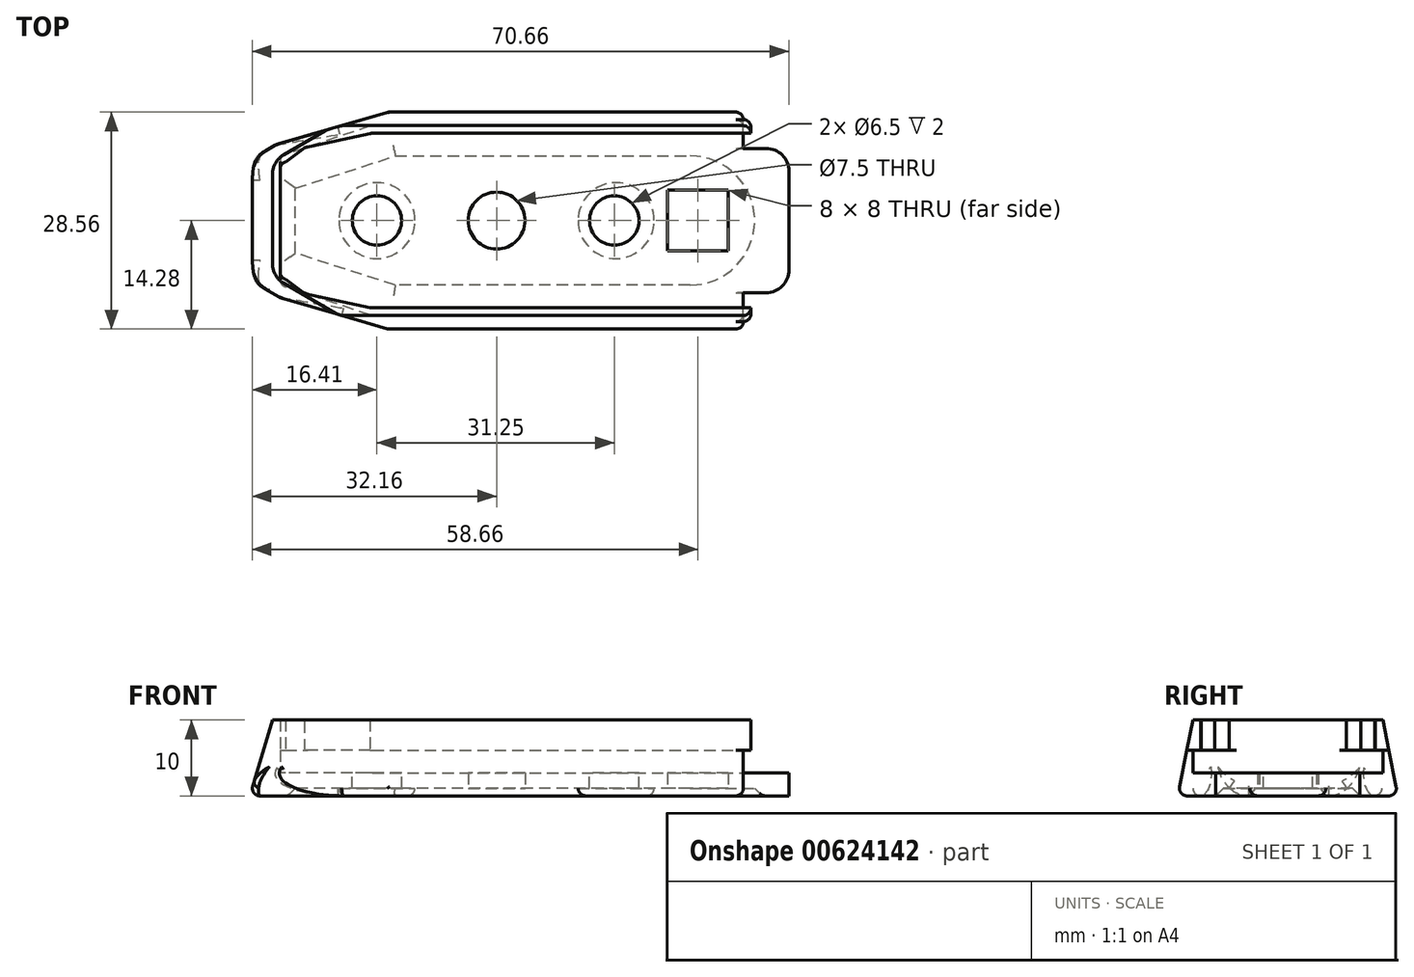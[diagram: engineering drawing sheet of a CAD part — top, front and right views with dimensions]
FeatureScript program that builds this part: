
annotation { "Feature Type Name" : "Feature", "Feature Type Description" : "" }
export const myFeature = defineFeature(function(context is Context, id is Id, definition is map)
    precondition{}
    {
        {
            var Q0;
            Q0=qCreatedBy(makeId("Top.planeOp"),FACE);
            var sketch = newSketch(context, id + "F0", { "sketchPlane" : qUnion([Q0])});
            skLineSegment(sketch, "E0.bottom", {"start": v(28.5, 14.5) * mm, "end": v(-16.5, 14.5) * mm});
            skLineSegment(sketch, "E0.left", {"start": v(35.5, 9.5) * mm, "end": v(35.5, 0) * mm});
            skLineSegment(sketch, "E0.right", {"start": v(-35.5, 9) * mm, "end": v(-35.5, 0) * mm});
            skPoint(sketch, "E0.middle", {"position": v(0, 0) * mm});
            skLineSegment(sketch, "E1", {"start": v(35.5, 0) * mm, "end": v(35.5, 9.5) * mm});
            skPoint(sketch, "E2.orphan", {"position": v(35.5, -14.5) * mm});
            skLineSegment(sketch, "E3", {"start": v(35.5, 9.5) * mm, "end": v(28.5, 9.5) * mm});
            skLineSegment(sketch, "E4", {"start": v(28.5, 9.5) * mm, "end": v(28.5, 14.5) * mm});
            skLineSegment(sketch, "E5", {"start": v(-35.5, 0) * mm, "end": v(-35.5, 9) * mm});
            skLineSegment(sketch, "E6", {"start": v(-35.5, 9) * mm, "end": v(-16.5, 14.5) * mm});
            skPoint(sketch, "E7.orphan", {"position": v(-35.5, 14.5) * mm});
            skPoint(sketch, "E8.orphan", {"position": v(-35.5, -14.5) * mm});
            skPoint(sketch, "E9.orphan", {"position": v(35.5, 14.5) * mm});
            skLineSegment(sketch, "E10.MirrorCS", {"start": v(-35.5, 0) * mm, "end": v(-35.5, -9) * mm});
            skLineSegment(sketch, "E11.MirrorCS", {"start": v(-35.5, -9) * mm, "end": v(-16.5, -14.5) * mm});
            skLineSegment(sketch, "E12.MirrorCS", {"start": v(28.5, -14.5) * mm, "end": v(-16.5, -14.5) * mm});
            skLineSegment(sketch, "E13.MirrorCS", {"start": v(28.5, -9.5) * mm, "end": v(28.5, -14.5) * mm});
            skLineSegment(sketch, "E14.MirrorCS", {"start": v(35.5, -9.5) * mm, "end": v(28.5, -9.5) * mm});
            skLineSegment(sketch, "E15.MirrorCS", {"start": v(35.5, 0) * mm, "end": v(35.5, -9.5) * mm});
            skSolve(sketch);
        }
        {
            var Q0;
            Q0 = qSketchRegion(id + "F0", true);
            extrude(context, id + "F1", {"entities" : qUnion([Q0]), "depth" : 3 * mm, "offsetDistance" : 25 * mm});
        }
        {
            var Q0;
            Q0=makeQuery(id+"F1.opExtrude","CAP_FACE",FACE,{"disambiguationData":[OSD([sQuery(id+"F0.wireOp",EDGE,"E1"),sQuery(id+"F0.wireOp",EDGE,"E3"),sQuery(id+"F0.wireOp",EDGE,"E4"),sQuery(id+"F0.wireOp",EDGE,"E0.bottom"),sQuery(id+"F0.wireOp",EDGE,"E5"),sQuery(id+"F0.wireOp",EDGE,"E6"),sQuery(id+"F0.wireOp",EDGE,"E10.MirrorCS"),sQuery(id+"F0.wireOp",EDGE,"E11.MirrorCS"),sQuery(id+"F0.wireOp",EDGE,"E12.MirrorCS"),sQuery(id+"F0.wireOp",EDGE,"E13.MirrorCS"),sQuery(id+"F0.wireOp",EDGE,"E14.MirrorCS"),sQuery(id+"F0.wireOp",EDGE,"E15.MirrorCS")])],"isStart":true});
            var sketch = newSketch(context, id + "F2", { "sketchPlane" : qUnion([Q0])});
            skPoint(sketch, "E16.endSnap0", {"position": v(-35.5, 0) * mm});
            skLineSegment(sketch, "E17", {"start": v(-30.5, 0) * mm, "end": v(-30.5, 5) * mm});
            skLineSegment(sketch, "E18", {"start": v(-30.5, 5) * mm, "end": v(-16.5, 9.5) * mm});
            skPoint(sketch, "E16.start.orphan", {"position": v(-35.5, 0) * mm});
            skLineSegment(sketch, "E19", {"start": v(-16.5, 9.5) * mm, "end": v(22.5, 9.5) * mm});
            skLineSegment(sketch, "E20.MirrorCS", {"start": v(-30.5, 0) * mm, "end": v(-30.5, -5) * mm});
            skLineSegment(sketch, "E21.MirrorCS", {"start": v(-30.5, -5) * mm, "end": v(-16.5, -9.5) * mm});
            skLineSegment(sketch, "E22.MirrorCS", {"start": v(-16.5, -9.5) * mm, "end": v(22.5, -9.5) * mm});
            skPoint(sketch, "E23.endSnap0", {"position": v(35.5, 0) * mm});
            skArc(sketch, "E24", {"start": v(22.5, -9.5) * mm, "mid": v(32, 0) * mm, "end": v(22.5, 9.5) * mm});
            skPoint(sketch, "E23.end.orphan", {"position": v(32, 0) * mm});
            skPoint(sketch, "E23.start.orphan", {"position": v(35.5, 0) * mm});
            skSolve(sketch);
        }
        {
            var Q0;
            Q0 = qSketchRegion(id + "F2", true);
            extrude(context, id + "F3", {"entities" : qUnion([Q0]), "operationType" : NewBodyOperationType.REMOVE, "oppositeDirection" : true, "depth" : 1 * mm, "offsetDistance" : 25 * mm});
        }
        {
            var Q0;
            Q0=makeQuery(id+"F3.boolean.opBoolean","COPY",EDGE,{"derivedFrom":makeQuery(id+"F3.opExtrude","CAP_EDGE",EDGE,{"disambiguationData":[OSD([sQuery(id+"F2.wireOp",EDGE,"E17"),sQuery(id+"F2.wireOp",EDGE,"E20.MirrorCS")])],"isStart":false})});
            var Q1;
            Q1=makeQuery(id+"F3.boolean.opBoolean","COPY",EDGE,{"derivedFrom":makeQuery(id+"F3.opExtrude","CAP_EDGE",EDGE,{"disambiguationData":[OSD([sQuery(id+"F2.wireOp",EDGE,"E18")])],"isStart":false})});
            var Q2;
            Q2=makeQuery(id+"F3.boolean.opBoolean","COPY",EDGE,{"derivedFrom":makeQuery(id+"F3.opExtrude","CAP_EDGE",EDGE,{"disambiguationData":[OSD([sQuery(id+"F2.wireOp",EDGE,"E21.MirrorCS")])],"isStart":false})});
            var Q3;
            Q3=makeQuery(id+"F3.boolean.opBoolean","COPY",EDGE,{"derivedFrom":makeQuery(id+"F3.opExtrude","CAP_EDGE",EDGE,{"disambiguationData":[OSD([sQuery(id+"F2.wireOp",EDGE,"E19")])],"isStart":false})});
            var Q4;
            Q4=makeQuery(id+"F3.boolean.opBoolean","COPY",EDGE,{"derivedFrom":makeQuery(id+"F3.opExtrude","CAP_EDGE",EDGE,{"disambiguationData":[OSD([sQuery(id+"F2.wireOp",EDGE,"E22.MirrorCS")])],"isStart":false})});
            var Q5;
            Q5=makeQuery(id+"F3.boolean.opBoolean","COPY",EDGE,{"derivedFrom":makeQuery(id+"F3.opExtrude","CAP_EDGE",EDGE,{"disambiguationData":[OSD([sQuery(id+"F2.wireOp",EDGE,"E24")])],"isStart":false})});
            chamfer(context, id + "F4", {"entities" : qUnion([Q0, Q1, Q2, Q3, Q4, Q5]), "width" : 1 * mm, "tangentPropagation" : true});
        }
        {
            var Q0;
            Q0=makeQuery(id+"F3.boolean.opBoolean","COPY",FACE,{"derivedFrom":makeQuery(id+"F3.opExtrude","CAP_FACE",FACE,{"disambiguationData":[OSD([sQuery(id+"F2.wireOp",EDGE,"E17"),sQuery(id+"F2.wireOp",EDGE,"E18"),sQuery(id+"F2.wireOp",EDGE,"E19"),sQuery(id+"F2.wireOp",EDGE,"E20.MirrorCS"),sQuery(id+"F2.wireOp",EDGE,"E21.MirrorCS"),sQuery(id+"F2.wireOp",EDGE,"E22.MirrorCS"),sQuery(id+"F2.wireOp",EDGE,"E24")])],"isStart":false})});
            var sketch = newSketch(context, id + "F5", { "sketchPlane" : qUnion([Q0])});
            skLineSegment(sketch, "E25", {"start": v(35.5, 0) * mm, "end": v(27.5, 0) * mm});
            skPoint(sketch, "E25.endSnap0", {"position": v(31, 0) * mm});
            skPoint(sketch, "E26.0.1.end.orphan", {"position": v(28.5, 14.5) * mm});
            skPoint(sketch, "E26.0.0.end.orphan", {"position": v(28.5, 9.5) * mm});
            skPoint(sketch, "E27.orphan", {"position": v(35.5, 9.5) * mm});
            skPoint(sketch, "E26.0.8.end.orphan", {"position": v(35.5, -9.5) * mm});
            skPoint(sketch, "E26.0.7.end.orphan", {"position": v(28.5, -9.5) * mm});
            skPoint(sketch, "E26.0.6.end.orphan", {"position": v(28.5, -14.5) * mm});
            skPoint(sketch, "E26.0.5.end.orphan", {"position": v(-16.5, -14.5) * mm});
            skPoint(sketch, "E26.0.4.end.orphan", {"position": v(-35.5, -9) * mm});
            skPoint(sketch, "E26.0.3.end.orphan", {"position": v(-35.5, 9) * mm});
            skPoint(sketch, "E26.0.3.start.orphan", {"position": v(-16.5, 14.5) * mm});
            skLineSegment(sketch, "E28", {"start": v(27.5, 0) * mm, "end": v(27.5, 4) * mm});
            skLineSegment(sketch, "E29", {"start": v(27.5, 4) * mm, "end": v(19.5, 4) * mm});
            skLineSegment(sketch, "E30", {"start": v(19.5, 4) * mm, "end": v(19.5, -4) * mm});
            skLineSegment(sketch, "E31", {"start": v(19.5, -4) * mm, "end": v(27.5, -4) * mm});
            skLineSegment(sketch, "E32", {"start": v(27.5, -4) * mm, "end": v(27.5, 0) * mm});
            skLineSegment(sketch, "E33", {"start": v(19.5, 0) * mm, "end": v(-3, 0) * mm});
            skCircle(sketch, "E34", {"center": v(-3, 0) * mm, "radius": 3.75 * mm});
            skSolve(sketch);
        }
        {
            var Q0;
            Q0 = qSketchRegion(id + "F5", true);
            extrude(context, id + "F6", {"entities" : qUnion([Q0]), "operationType" : NewBodyOperationType.REMOVE, "endBound" : BoundingType.THROUGH_ALL, "oppositeDirection" : true, "depth" : 25 * mm, "offsetDistance" : 25 * mm});
        }
        {
            var Q0;
            Q0=makeQuery(id+"F3.boolean.opBoolean","COPY",FACE,{"derivedFrom":makeQuery(id+"F3.opExtrude","CAP_FACE",FACE,{"disambiguationData":[OSD([sQuery(id+"F2.wireOp",EDGE,"E17"),sQuery(id+"F2.wireOp",EDGE,"E18"),sQuery(id+"F2.wireOp",EDGE,"E19"),sQuery(id+"F2.wireOp",EDGE,"E20.MirrorCS"),sQuery(id+"F2.wireOp",EDGE,"E21.MirrorCS"),sQuery(id+"F2.wireOp",EDGE,"E22.MirrorCS"),sQuery(id+"F2.wireOp",EDGE,"E24")])],"isStart":false})});
            var sketch = newSketch(context, id + "F7", { "sketchPlane" : qUnion([Q0])});
            skLineSegment(sketch, "E35", {"start": v(0.75, 0) * mm, "end": v(12.75, 0) * mm});
            skCircle(sketch, "E36", {"center": v(12.75, 0) * mm, "radius": 5 * mm});
            skLineSegment(sketch, "E37", {"start": v(-6.75, 0) * mm, "end": v(-18.75, 0) * mm});
            skCircle(sketch, "E38", {"center": v(-18.75, 0) * mm, "radius": 5 * mm});
            skSolve(sketch);
        }
        {
            var Q0;
            Q0 = qSketchRegion(id + "F7", true);
            var Q1;
            Q1=makeQuery(id+"F1.opExtrude","CAP_FACE",FACE,{"disambiguationData":[OSD([sQuery(id+"F0.wireOp",EDGE,"E1"),sQuery(id+"F0.wireOp",EDGE,"E3"),sQuery(id+"F0.wireOp",EDGE,"E4"),sQuery(id+"F0.wireOp",EDGE,"E0.bottom"),sQuery(id+"F0.wireOp",EDGE,"E5"),sQuery(id+"F0.wireOp",EDGE,"E6"),sQuery(id+"F0.wireOp",EDGE,"E10.MirrorCS"),sQuery(id+"F0.wireOp",EDGE,"E11.MirrorCS"),sQuery(id+"F0.wireOp",EDGE,"E12.MirrorCS"),sQuery(id+"F0.wireOp",EDGE,"E13.MirrorCS"),sQuery(id+"F0.wireOp",EDGE,"E14.MirrorCS"),sQuery(id+"F0.wireOp",EDGE,"E15.MirrorCS")])],"isStart":true});
            extrude(context, id + "F8", {"entities" : qUnion([Q0]), "operationType" : NewBodyOperationType.ADD, "endBound" : BoundingType.UP_TO_SURFACE, "depth" : 25 * mm, "endBoundEntityFace" : qUnion([Q1]), "offsetDistance" : 25 * mm});
        }
        {
            var Q0;
            Q0=makeQuery(id+"F8.opExtrude","CAP_EDGE",EDGE,{"disambiguationData":[OSD([sQuery(id+"F7.wireOp",EDGE,"E38")])],"isStart":false});
            var Q1;
            Q1=makeQuery(id+"F8.opExtrude","CAP_EDGE",EDGE,{"disambiguationData":[OSD([sQuery(id+"F7.wireOp",EDGE,"E36")])],"isStart":false});
            var Q2;
            Q2=makeQuery(id+"F4.opChamfer","BLEND_EDGE",EDGE,{"blendedFrom":[makeQuery(id+"F3.boolean.opBoolean","COPY",EDGE,{"derivedFrom":makeQuery(id+"F3.opExtrude","CAP_EDGE",EDGE,{"disambiguationData":[OSD([sQuery(id+"F2.wireOp",EDGE,"E19")])],"isStart":false})}),makeQuery(id+"F1.opExtrude","CAP_FACE",FACE,{"disambiguationData":[OSD([sQuery(id+"F0.wireOp",EDGE,"E1"),sQuery(id+"F0.wireOp",EDGE,"E3"),sQuery(id+"F0.wireOp",EDGE,"E4"),sQuery(id+"F0.wireOp",EDGE,"E0.bottom"),sQuery(id+"F0.wireOp",EDGE,"E5"),sQuery(id+"F0.wireOp",EDGE,"E6"),sQuery(id+"F0.wireOp",EDGE,"E10.MirrorCS"),sQuery(id+"F0.wireOp",EDGE,"E11.MirrorCS"),sQuery(id+"F0.wireOp",EDGE,"E12.MirrorCS"),sQuery(id+"F0.wireOp",EDGE,"E13.MirrorCS"),sQuery(id+"F0.wireOp",EDGE,"E14.MirrorCS"),sQuery(id+"F0.wireOp",EDGE,"E15.MirrorCS")])],"isStart":true})],"blendedInto":[makeQuery(id+"F1.opExtrude","CAP_FACE",FACE,{"disambiguationData":[OSD([sQuery(id+"F0.wireOp",EDGE,"E1"),sQuery(id+"F0.wireOp",EDGE,"E3"),sQuery(id+"F0.wireOp",EDGE,"E4"),sQuery(id+"F0.wireOp",EDGE,"E0.bottom"),sQuery(id+"F0.wireOp",EDGE,"E5"),sQuery(id+"F0.wireOp",EDGE,"E6"),sQuery(id+"F0.wireOp",EDGE,"E10.MirrorCS"),sQuery(id+"F0.wireOp",EDGE,"E11.MirrorCS"),sQuery(id+"F0.wireOp",EDGE,"E12.MirrorCS"),sQuery(id+"F0.wireOp",EDGE,"E13.MirrorCS"),sQuery(id+"F0.wireOp",EDGE,"E14.MirrorCS"),sQuery(id+"F0.wireOp",EDGE,"E15.MirrorCS")])],"isStart":true})]});
            var Q3;
            Q3=makeQuery(id+"F4.opChamfer","BLEND_EDGE",EDGE,{"blendedFrom":[makeQuery(id+"F3.boolean.opBoolean","COPY",EDGE,{"derivedFrom":makeQuery(id+"F3.opExtrude","CAP_EDGE",EDGE,{"disambiguationData":[OSD([sQuery(id+"F2.wireOp",EDGE,"E18")])],"isStart":false})}),makeQuery(id+"F1.opExtrude","CAP_FACE",FACE,{"disambiguationData":[OSD([sQuery(id+"F0.wireOp",EDGE,"E1"),sQuery(id+"F0.wireOp",EDGE,"E3"),sQuery(id+"F0.wireOp",EDGE,"E4"),sQuery(id+"F0.wireOp",EDGE,"E0.bottom"),sQuery(id+"F0.wireOp",EDGE,"E5"),sQuery(id+"F0.wireOp",EDGE,"E6"),sQuery(id+"F0.wireOp",EDGE,"E10.MirrorCS"),sQuery(id+"F0.wireOp",EDGE,"E11.MirrorCS"),sQuery(id+"F0.wireOp",EDGE,"E12.MirrorCS"),sQuery(id+"F0.wireOp",EDGE,"E13.MirrorCS"),sQuery(id+"F0.wireOp",EDGE,"E14.MirrorCS"),sQuery(id+"F0.wireOp",EDGE,"E15.MirrorCS")])],"isStart":true})],"blendedInto":[makeQuery(id+"F1.opExtrude","CAP_FACE",FACE,{"disambiguationData":[OSD([sQuery(id+"F0.wireOp",EDGE,"E1"),sQuery(id+"F0.wireOp",EDGE,"E3"),sQuery(id+"F0.wireOp",EDGE,"E4"),sQuery(id+"F0.wireOp",EDGE,"E0.bottom"),sQuery(id+"F0.wireOp",EDGE,"E5"),sQuery(id+"F0.wireOp",EDGE,"E6"),sQuery(id+"F0.wireOp",EDGE,"E10.MirrorCS"),sQuery(id+"F0.wireOp",EDGE,"E11.MirrorCS"),sQuery(id+"F0.wireOp",EDGE,"E12.MirrorCS"),sQuery(id+"F0.wireOp",EDGE,"E13.MirrorCS"),sQuery(id+"F0.wireOp",EDGE,"E14.MirrorCS"),sQuery(id+"F0.wireOp",EDGE,"E15.MirrorCS")])],"isStart":true})]});
            var Q4;
            Q4=makeQuery(id+"F4.opChamfer","BLEND_EDGE",EDGE,{"blendedFrom":[makeQuery(id+"F3.boolean.opBoolean","COPY",EDGE,{"derivedFrom":makeQuery(id+"F3.opExtrude","CAP_EDGE",EDGE,{"disambiguationData":[OSD([sQuery(id+"F2.wireOp",EDGE,"E17"),sQuery(id+"F2.wireOp",EDGE,"E20.MirrorCS")])],"isStart":false})}),makeQuery(id+"F1.opExtrude","CAP_FACE",FACE,{"disambiguationData":[OSD([sQuery(id+"F0.wireOp",EDGE,"E1"),sQuery(id+"F0.wireOp",EDGE,"E3"),sQuery(id+"F0.wireOp",EDGE,"E4"),sQuery(id+"F0.wireOp",EDGE,"E0.bottom"),sQuery(id+"F0.wireOp",EDGE,"E5"),sQuery(id+"F0.wireOp",EDGE,"E6"),sQuery(id+"F0.wireOp",EDGE,"E10.MirrorCS"),sQuery(id+"F0.wireOp",EDGE,"E11.MirrorCS"),sQuery(id+"F0.wireOp",EDGE,"E12.MirrorCS"),sQuery(id+"F0.wireOp",EDGE,"E13.MirrorCS"),sQuery(id+"F0.wireOp",EDGE,"E14.MirrorCS"),sQuery(id+"F0.wireOp",EDGE,"E15.MirrorCS")])],"isStart":true})],"blendedInto":[makeQuery(id+"F1.opExtrude","CAP_FACE",FACE,{"disambiguationData":[OSD([sQuery(id+"F0.wireOp",EDGE,"E1"),sQuery(id+"F0.wireOp",EDGE,"E3"),sQuery(id+"F0.wireOp",EDGE,"E4"),sQuery(id+"F0.wireOp",EDGE,"E0.bottom"),sQuery(id+"F0.wireOp",EDGE,"E5"),sQuery(id+"F0.wireOp",EDGE,"E6"),sQuery(id+"F0.wireOp",EDGE,"E10.MirrorCS"),sQuery(id+"F0.wireOp",EDGE,"E11.MirrorCS"),sQuery(id+"F0.wireOp",EDGE,"E12.MirrorCS"),sQuery(id+"F0.wireOp",EDGE,"E13.MirrorCS"),sQuery(id+"F0.wireOp",EDGE,"E14.MirrorCS"),sQuery(id+"F0.wireOp",EDGE,"E15.MirrorCS")])],"isStart":true})]});
            var Q5;
            Q5=makeQuery(id+"F4.opChamfer","BLEND_EDGE",EDGE,{"blendedFrom":[makeQuery(id+"F3.boolean.opBoolean","COPY",EDGE,{"derivedFrom":makeQuery(id+"F3.opExtrude","CAP_EDGE",EDGE,{"disambiguationData":[OSD([sQuery(id+"F2.wireOp",EDGE,"E21.MirrorCS")])],"isStart":false})}),makeQuery(id+"F1.opExtrude","CAP_FACE",FACE,{"disambiguationData":[OSD([sQuery(id+"F0.wireOp",EDGE,"E1"),sQuery(id+"F0.wireOp",EDGE,"E3"),sQuery(id+"F0.wireOp",EDGE,"E4"),sQuery(id+"F0.wireOp",EDGE,"E0.bottom"),sQuery(id+"F0.wireOp",EDGE,"E5"),sQuery(id+"F0.wireOp",EDGE,"E6"),sQuery(id+"F0.wireOp",EDGE,"E10.MirrorCS"),sQuery(id+"F0.wireOp",EDGE,"E11.MirrorCS"),sQuery(id+"F0.wireOp",EDGE,"E12.MirrorCS"),sQuery(id+"F0.wireOp",EDGE,"E13.MirrorCS"),sQuery(id+"F0.wireOp",EDGE,"E14.MirrorCS"),sQuery(id+"F0.wireOp",EDGE,"E15.MirrorCS")])],"isStart":true})],"blendedInto":[makeQuery(id+"F1.opExtrude","CAP_FACE",FACE,{"disambiguationData":[OSD([sQuery(id+"F0.wireOp",EDGE,"E1"),sQuery(id+"F0.wireOp",EDGE,"E3"),sQuery(id+"F0.wireOp",EDGE,"E4"),sQuery(id+"F0.wireOp",EDGE,"E0.bottom"),sQuery(id+"F0.wireOp",EDGE,"E5"),sQuery(id+"F0.wireOp",EDGE,"E6"),sQuery(id+"F0.wireOp",EDGE,"E10.MirrorCS"),sQuery(id+"F0.wireOp",EDGE,"E11.MirrorCS"),sQuery(id+"F0.wireOp",EDGE,"E12.MirrorCS"),sQuery(id+"F0.wireOp",EDGE,"E13.MirrorCS"),sQuery(id+"F0.wireOp",EDGE,"E14.MirrorCS"),sQuery(id+"F0.wireOp",EDGE,"E15.MirrorCS")])],"isStart":true})]});
            var Q6;
            Q6=makeQuery(id+"F4.opChamfer","BLEND_EDGE",EDGE,{"blendedFrom":[makeQuery(id+"F3.boolean.opBoolean","COPY",EDGE,{"derivedFrom":makeQuery(id+"F3.opExtrude","CAP_EDGE",EDGE,{"disambiguationData":[OSD([sQuery(id+"F2.wireOp",EDGE,"E22.MirrorCS")])],"isStart":false})}),makeQuery(id+"F1.opExtrude","CAP_FACE",FACE,{"disambiguationData":[OSD([sQuery(id+"F0.wireOp",EDGE,"E1"),sQuery(id+"F0.wireOp",EDGE,"E3"),sQuery(id+"F0.wireOp",EDGE,"E4"),sQuery(id+"F0.wireOp",EDGE,"E0.bottom"),sQuery(id+"F0.wireOp",EDGE,"E5"),sQuery(id+"F0.wireOp",EDGE,"E6"),sQuery(id+"F0.wireOp",EDGE,"E10.MirrorCS"),sQuery(id+"F0.wireOp",EDGE,"E11.MirrorCS"),sQuery(id+"F0.wireOp",EDGE,"E12.MirrorCS"),sQuery(id+"F0.wireOp",EDGE,"E13.MirrorCS"),sQuery(id+"F0.wireOp",EDGE,"E14.MirrorCS"),sQuery(id+"F0.wireOp",EDGE,"E15.MirrorCS")])],"isStart":true})],"blendedInto":[makeQuery(id+"F1.opExtrude","CAP_FACE",FACE,{"disambiguationData":[OSD([sQuery(id+"F0.wireOp",EDGE,"E1"),sQuery(id+"F0.wireOp",EDGE,"E3"),sQuery(id+"F0.wireOp",EDGE,"E4"),sQuery(id+"F0.wireOp",EDGE,"E0.bottom"),sQuery(id+"F0.wireOp",EDGE,"E5"),sQuery(id+"F0.wireOp",EDGE,"E6"),sQuery(id+"F0.wireOp",EDGE,"E10.MirrorCS"),sQuery(id+"F0.wireOp",EDGE,"E11.MirrorCS"),sQuery(id+"F0.wireOp",EDGE,"E12.MirrorCS"),sQuery(id+"F0.wireOp",EDGE,"E13.MirrorCS"),sQuery(id+"F0.wireOp",EDGE,"E14.MirrorCS"),sQuery(id+"F0.wireOp",EDGE,"E15.MirrorCS")])],"isStart":true})]});
            var Q7;
            Q7=makeQuery(id+"F4.opChamfer","BLEND_EDGE",EDGE,{"blendedFrom":[makeQuery(id+"F3.boolean.opBoolean","COPY",EDGE,{"derivedFrom":makeQuery(id+"F3.opExtrude","CAP_EDGE",EDGE,{"disambiguationData":[OSD([sQuery(id+"F2.wireOp",EDGE,"E24")])],"isStart":false})}),makeQuery(id+"F1.opExtrude","CAP_FACE",FACE,{"disambiguationData":[OSD([sQuery(id+"F0.wireOp",EDGE,"E1"),sQuery(id+"F0.wireOp",EDGE,"E3"),sQuery(id+"F0.wireOp",EDGE,"E4"),sQuery(id+"F0.wireOp",EDGE,"E0.bottom"),sQuery(id+"F0.wireOp",EDGE,"E5"),sQuery(id+"F0.wireOp",EDGE,"E6"),sQuery(id+"F0.wireOp",EDGE,"E10.MirrorCS"),sQuery(id+"F0.wireOp",EDGE,"E11.MirrorCS"),sQuery(id+"F0.wireOp",EDGE,"E12.MirrorCS"),sQuery(id+"F0.wireOp",EDGE,"E13.MirrorCS"),sQuery(id+"F0.wireOp",EDGE,"E14.MirrorCS"),sQuery(id+"F0.wireOp",EDGE,"E15.MirrorCS")])],"isStart":true})],"blendedInto":[makeQuery(id+"F1.opExtrude","CAP_FACE",FACE,{"disambiguationData":[OSD([sQuery(id+"F0.wireOp",EDGE,"E1"),sQuery(id+"F0.wireOp",EDGE,"E3"),sQuery(id+"F0.wireOp",EDGE,"E4"),sQuery(id+"F0.wireOp",EDGE,"E0.bottom"),sQuery(id+"F0.wireOp",EDGE,"E5"),sQuery(id+"F0.wireOp",EDGE,"E6"),sQuery(id+"F0.wireOp",EDGE,"E10.MirrorCS"),sQuery(id+"F0.wireOp",EDGE,"E11.MirrorCS"),sQuery(id+"F0.wireOp",EDGE,"E12.MirrorCS"),sQuery(id+"F0.wireOp",EDGE,"E13.MirrorCS"),sQuery(id+"F0.wireOp",EDGE,"E14.MirrorCS"),sQuery(id+"F0.wireOp",EDGE,"E15.MirrorCS")])],"isStart":true})]});
            fillet(context, id + "F9", {"entities" : qUnion([Q0, Q1, Q2, Q3, Q4, Q5, Q6, Q7]), "radius" : 1 * mm, "tangentPropagation" : true, "allowEdgeOverflow" : false});
        }
        {
            var Q0;
            Q0=makeQuery(id+"F1.opExtrude","CAP_FACE",FACE,{"disambiguationData":[OSD([sQuery(id+"F0.wireOp",EDGE,"E1"),sQuery(id+"F0.wireOp",EDGE,"E3"),sQuery(id+"F0.wireOp",EDGE,"E4"),sQuery(id+"F0.wireOp",EDGE,"E0.bottom"),sQuery(id+"F0.wireOp",EDGE,"E5"),sQuery(id+"F0.wireOp",EDGE,"E6"),sQuery(id+"F0.wireOp",EDGE,"E10.MirrorCS"),sQuery(id+"F0.wireOp",EDGE,"E11.MirrorCS"),sQuery(id+"F0.wireOp",EDGE,"E12.MirrorCS"),sQuery(id+"F0.wireOp",EDGE,"E13.MirrorCS"),sQuery(id+"F0.wireOp",EDGE,"E14.MirrorCS"),sQuery(id+"F0.wireOp",EDGE,"E15.MirrorCS")])],"isStart":false});
            var sketch = newSketch(context, id + "F10", { "sketchPlane" : qUnion([Q0])});
            skSolve(sketch);
        }
        {
            var Q0;
            {var subQ9=sQuery(id+"F0.wireOp",EDGE,"E3");Q0=makeQuery(id+"F10.imprint","IMPRINT",FACE,{"disambiguationData":[TD([[makeQuery(id+"F10.imprint","IMPRINT",EDGE,{"derivedFrom":makeQuery(id+"F1.opExtrude","CAP_EDGE",EDGE,{"disambiguationData":[OSD([subQ9])],"isStart":false})}),1.0]])]});}
            var sketch = newSketch(context, id + "F11", { "sketchPlane" : qUnion([Q0])});
            skLineSegment(sketch, "E39.0", {"start": v(19.5, 4) * mm, "end": v(19.5, -4) * mm});
            skLineSegment(sketch, "E40", {"start": v(19.5, 0) * mm, "end": v(12.5, 0) * mm});
            skPoint(sketch, "E40.endSnap0", {"position": v(19.5, 0) * mm});
            skCircle(sketch, "E41", {"center": v(12.5, 0) * mm, "radius": 3.25 * mm});
            skCircle(sketch, "E42.0", {"center": v(-3, 0) * mm, "radius": 3.75 * mm});
            skLineSegment(sketch, "E43", {"start": v(-6.75, 0) * mm, "end": v(-18.75, 0) * mm});
            skCircle(sketch, "E44", {"center": v(-18.75, 0) * mm, "radius": 3.25 * mm});
            skSolve(sketch);
        }
        {
            var Q0;
            Q0 = qSketchRegion(id + "F11", true);
            extrude(context, id + "F12", {"entities" : qUnion([Q0]), "operationType" : NewBodyOperationType.REMOVE, "oppositeDirection" : true, "depth" : 2 * mm, "offsetDistance" : 25 * mm});
        }
        {
            var Q0;
            {var subQ9=sQuery(id+"F0.wireOp",EDGE,"E3");Q0=makeQuery(id+"F10.imprint","IMPRINT",FACE,{"disambiguationData":[TD([[makeQuery(id+"F10.imprint","IMPRINT",EDGE,{"derivedFrom":makeQuery(id+"F1.opExtrude","CAP_EDGE",EDGE,{"disambiguationData":[OSD([subQ9])],"isStart":false})}),1.0]])]});}
            var sketch = newSketch(context, id + "F13", { "sketchPlane" : qUnion([Q0])});
            skLineSegment(sketch, "E45.0.3", {"start": v(28.5, 9.5) * mm, "end": v(28.5, 14.5) * mm});
            skLineSegment(sketch, "E45.0.4", {"start": v(28.5, 14.5) * mm, "end": v(-16.5, 14.5) * mm});
            skLineSegment(sketch, "E45.0.5", {"start": v(-16.5, 14.5) * mm, "end": v(-35.5, 9) * mm});
            skLineSegment(sketch, "E45.0.6", {"start": v(-35.5, 9) * mm, "end": v(-35.5, -9) * mm});
            skLineSegment(sketch, "E45.0.7", {"start": v(-35.5, -9) * mm, "end": v(-16.5, -14.5) * mm});
            skLineSegment(sketch, "E45.0.8", {"start": v(-16.5, -14.5) * mm, "end": v(28.5, -14.5) * mm});
            skLineSegment(sketch, "E45.0.9", {"start": v(28.5, -14.5) * mm, "end": v(28.5, -9.5) * mm});
            skLineSegment(sketch, "E46", {"start": v(28.5, 9.5) * mm, "end": v(28.5, -9.5) * mm});
            skPoint(sketch, "E45.0.1.end.orphan", {"position": v(35.5, 9.5) * mm});
            skPoint(sketch, "E45.0.0.end.orphan", {"position": v(35.5, -9.5) * mm});
            skSolve(sketch);
        }
        {
            var Q0;
            Q0 = qSketchRegion(id + "F13", true);
            extrude(context, id + "F14", {"entities" : qUnion([Q0]), "operationType" : NewBodyOperationType.ADD, "depth" : 7 * mm, "offsetDistance" : 25 * mm});
        }
        {
            var Q0;
            Q0=makeQuery(id+"F14.boolean.opBoolean","MERGE",FACE,{"derivedFrom":[makeQuery(id+"F1.opExtrude","SWEPT_FACE",FACE,{"disambiguationData":[OSD([sQuery(id+"F0.wireOp",EDGE,"E4")])]}),makeQuery(id+"F1.opExtrude","SWEPT_FACE",FACE,{"disambiguationData":[OSD([sQuery(id+"F0.wireOp",EDGE,"E13.MirrorCS")])]}),makeQuery(id+"F14.opExtrude","SWEPT_FACE",FACE,{"disambiguationData":[OSD([sQuery(id+"F13.wireOp",EDGE,"E45.0.3"),sQuery(id+"F13.wireOp",EDGE,"E45.0.9"),sQuery(id+"F13.wireOp",EDGE,"E46")])]})]});
            var sketch = newSketch(context, id + "F15", { "sketchPlane" : qUnion([Q0])});
            skLineSegment(sketch, "E47", {"start": v(0, 10) * mm, "end": v(11.5, 10) * mm});
            skLineSegment(sketch, "E48", {"start": v(11.5, 10) * mm, "end": v(11.5, 6) * mm});
            skLineSegment(sketch, "E49", {"start": v(11.5, 6) * mm, "end": v(12.5, 6) * mm});
            skLineSegment(sketch, "E50", {"start": v(12.5, 6) * mm, "end": v(12.5, 3) * mm});
            skLineSegment(sketch, "E51", {"start": v(12.5, 3) * mm, "end": v(9.5, 3) * mm});
            skLineSegment(sketch, "E52", {"start": v(14.5, 0) * mm, "end": v(14.5, 10) * mm});
            skLineSegment(sketch, "E53", {"start": v(9.5, 3) * mm, "end": v(0, 3) * mm});
            skLineSegment(sketch, "E54.MirrorCS", {"start": v(0, 10) * mm, "end": v(-11.5, 10) * mm});
            skLineSegment(sketch, "E55.MirrorCS", {"start": v(-12.5, 3) * mm, "end": v(-9.5, 3) * mm});
            skLineSegment(sketch, "E56.MirrorCS", {"start": v(-12.5, 6) * mm, "end": v(-12.5, 3) * mm});
            skLineSegment(sketch, "E57.MirrorCS", {"start": v(-11.5, 6) * mm, "end": v(-12.5, 6) * mm});
            skLineSegment(sketch, "E58.MirrorCS", {"start": v(-11.5, 10) * mm, "end": v(-11.5, 6) * mm});
            skLineSegment(sketch, "E59.MirrorCS", {"start": v(-9.5, 3) * mm, "end": v(0, 3) * mm});
            skPoint(sketch, "E60.MirrorCS.end.orphan", {"position": v(-14.5, 10) * mm});
            skPoint(sketch, "E60.MirrorCS.start.orphan", {"position": v(-14.5, 0) * mm});
            skPoint(sketch, "E61.MirrorCS.end.orphan", {"position": v(-11.5, 10) * mm});
            skLineSegment(sketch, "E62", {"start": v(12.5, 10) * mm, "end": v(14.5, 0) * mm});
            skLineSegment(sketch, "E63", {"start": v(12.5, 10) * mm, "end": v(14.5, 10) * mm});
            skLineSegment(sketch, "E64.MirrorCS", {"start": v(-12.5, 10) * mm, "end": v(-14.5, 10) * mm});
            skLineSegment(sketch, "E65.MirrorCS", {"start": v(-14.5, 0) * mm, "end": v(-14.5, 10) * mm});
            skLineSegment(sketch, "E66.MirrorCS", {"start": v(-12.5, 10) * mm, "end": v(-14.5, 0) * mm});
            skSolve(sketch);
        }
        {
            var Q0;
            Q0 = qSketchRegion(id + "F15", true);
            extrude(context, id + "F16", {"entities" : qUnion([Q0]), "operationType" : NewBodyOperationType.REMOVE, "oppositeDirection" : true, "depth" : 48 * mm, "offsetDistance" : 25 * mm});
        }
        {
            var Q0;
            {var subQ9=sQuery(id+"F0.wireOp",EDGE,"E3");Q0=makeQuery(id+"F10.imprint","IMPRINT",FACE,{"disambiguationData":[TD([[makeQuery(id+"F10.imprint","IMPRINT",EDGE,{"derivedFrom":makeQuery(id+"F1.opExtrude","CAP_EDGE",EDGE,{"disambiguationData":[OSD([subQ9])],"isStart":false})}),1.0]])]});}
            var sketch = newSketch(context, id + "F17", { "sketchPlane" : qUnion([Q0])});
            skLineSegment(sketch, "E67.0", {"start": v(-19.5, 10.5) * mm, "end": v(-19.5, 0) * mm});
            skLineSegment(sketch, "E68", {"start": v(-19.5, 0) * mm, "end": v(-19.5, 10.5) * mm});
            skPoint(sketch, "E69.orphan", {"position": v(-19.5, 11.5) * mm});
            skPoint(sketch, "E70.orphan", {"position": v(-19.5, -11.5) * mm});
            skPoint(sketch, "E71.endSnap0", {"position": v(-35.5, 0) * mm});
            skLineSegment(sketch, "E72", {"start": v(-31.5, 0) * mm, "end": v(-31.5, 7.5) * mm});
            skLineSegment(sketch, "E73", {"start": v(-31.5, 7.5) * mm, "end": v(-19.5, 10.5) * mm});
            skLineSegment(sketch, "E74.MirrorCS", {"start": v(-31.5, -7.5) * mm, "end": v(-19.5, -10.5) * mm});
            skLineSegment(sketch, "E75.MirrorCS", {"start": v(-19.5, 0) * mm, "end": v(-19.5, -10.5) * mm});
            skLineSegment(sketch, "E76.MirrorCS", {"start": v(-31.5, 0) * mm, "end": v(-31.5, -7.5) * mm});
            skPoint(sketch, "E77.orphan", {"position": v(-35.5, 9) * mm});
            skPoint(sketch, "E78.0.start.orphan", {"position": v(-35.5, -9) * mm});
            skPoint(sketch, "E71.start.orphan", {"position": v(-35.5, 0) * mm});
            skSolve(sketch);
        }
        {
            var Q0;
            Q0 = qSketchRegion(id + "F17", true);
            var Q1;
            Q1=makeQuery(id+"F16.boolean.opBoolean","MERGE",FACE,{"derivedFrom":[makeQuery(id+"F1.opExtrude","CAP_FACE",FACE,{"disambiguationData":[OSD([sQuery(id+"F0.wireOp",EDGE,"E1"),sQuery(id+"F0.wireOp",EDGE,"E3"),sQuery(id+"F0.wireOp",EDGE,"E4"),sQuery(id+"F0.wireOp",EDGE,"E0.bottom"),sQuery(id+"F0.wireOp",EDGE,"E5"),sQuery(id+"F0.wireOp",EDGE,"E6"),sQuery(id+"F0.wireOp",EDGE,"E10.MirrorCS"),sQuery(id+"F0.wireOp",EDGE,"E11.MirrorCS"),sQuery(id+"F0.wireOp",EDGE,"E12.MirrorCS"),sQuery(id+"F0.wireOp",EDGE,"E13.MirrorCS"),sQuery(id+"F0.wireOp",EDGE,"E14.MirrorCS"),sQuery(id+"F0.wireOp",EDGE,"E15.MirrorCS")])],"isStart":false}),makeQuery(id+"F16.opExtrude","SWEPT_FACE",FACE,{"disambiguationData":[OSD([sQuery(id+"F15.wireOp",EDGE,"E51"),sQuery(id+"F15.wireOp",EDGE,"E53"),sQuery(id+"F15.wireOp",EDGE,"E55.MirrorCS"),sQuery(id+"F15.wireOp",EDGE,"E59.MirrorCS")])]})]});
            extrude(context, id + "F18", {"entities" : qUnion([Q0]), "operationType" : NewBodyOperationType.REMOVE, "endBound" : BoundingType.UP_TO_NEXT, "depth" : 25 * mm, "endBoundEntityFace" : qUnion([Q1]), "offsetDistance" : 25 * mm});
        }
        {
            var Q0;
            {var subQ9=sQuery(id+"F0.wireOp",EDGE,"E3");Q0=makeQuery(id+"F10.imprint","IMPRINT",FACE,{"disambiguationData":[TD([[makeQuery(id+"F10.imprint","IMPRINT",EDGE,{"derivedFrom":makeQuery(id+"F1.opExtrude","CAP_EDGE",EDGE,{"disambiguationData":[OSD([subQ9])],"isStart":false})}),1.0]])]});}
            var sketch = newSketch(context, id + "F19", { "sketchPlane" : qUnion([Q0])});
            skLineSegment(sketch, "E79.0", {"start": v(-31.5, 7.5) * mm, "end": v(-19.5, 10.5) * mm});
            skLineSegment(sketch, "E80", {"start": v(-19.5, 10.5) * mm, "end": v(-19.5, 11.5) * mm});
            skLineSegment(sketch, "E81", {"start": v(-31.5, 7.5) * mm, "end": v(-31.5, 8.5) * mm});
            skPoint(sketch, "E82.0.start.orphan", {"position": v(-31.5, -7.5) * mm});
            skLineSegment(sketch, "E83", {"start": v(-31.5, 8.5) * mm, "end": v(-19.5, 11.5) * mm});
            skLineSegment(sketch, "E84.MirrorCS", {"start": v(-31.5, -7.5) * mm, "end": v(-19.5, -10.5) * mm});
            skLineSegment(sketch, "E85.MirrorCS", {"start": v(-31.5, -8.5) * mm, "end": v(-19.5, -11.5) * mm});
            skLineSegment(sketch, "E86.MirrorCS", {"start": v(-19.5, -10.5) * mm, "end": v(-19.5, -11.5) * mm});
            skLineSegment(sketch, "E87.MirrorCS", {"start": v(-31.5, -7.5) * mm, "end": v(-31.5, -8.5) * mm});
            skSolve(sketch);
        }
        {
            var Q0;
            Q0 = qSketchRegion(id + "F19", true);
            extrude(context, id + "F20", {"entities" : qUnion([Q0]), "operationType" : NewBodyOperationType.REMOVE, "depth" : 3 * mm, "offsetDistance" : 25 * mm});
        }
        {
            var Q0;
            Q0=makeQuery(id+"F16.boolean.opBoolean","COPY",FACE,{"derivedFrom":makeQuery(id+"F16.opExtrude","CAP_FACE",FACE,{"disambiguationData":[OSD([sQuery(id+"F15.wireOp",EDGE,"E64.MirrorCS"),sQuery(id+"F15.wireOp",EDGE,"E65.MirrorCS"),sQuery(id+"F15.wireOp",EDGE,"E66.MirrorCS")])],"isStart":false})});
            var sketch = newSketch(context, id + "F21", { "sketchPlane" : qUnion([Q0])});
            skLineSegment(sketch, "E88.0", {"start": v(-13.63, 10) * mm, "end": v(-13.63, 4.34) * mm});
            skLineSegment(sketch, "E89.0", {"start": v(-12.5, 10) * mm, "end": v(-13.63, 10) * mm});
            skLineSegment(sketch, "E90.0", {"start": v(-12.5, 10) * mm, "end": v(-13.63, 4.34) * mm});
            skSolve(sketch);
        }
        {
            var Q0;
            Q0 = qSketchRegion(id + "F21", true);
            var Q1;
            Q1=makeQuery(id+"F14.boolean.opBoolean","MERGE",FACE,{"derivedFrom":[makeQuery(id+"F1.opExtrude","SWEPT_FACE",FACE,{"disambiguationData":[OSD([sQuery(id+"F0.wireOp",EDGE,"E5"),sQuery(id+"F0.wireOp",EDGE,"E10.MirrorCS")])]}),makeQuery(id+"F14.opExtrude","SWEPT_FACE",FACE,{"disambiguationData":[OSD([sQuery(id+"F13.wireOp",EDGE,"E45.0.6")])]})]});
            extrude(context, id + "F22", {"entities" : qUnion([Q0]), "operationType" : NewBodyOperationType.REMOVE, "endBound" : BoundingType.UP_TO_SURFACE, "oppositeDirection" : true, "depth" : 25 * mm, "endBoundEntityFace" : qUnion([Q1]), "offsetDistance" : 25 * mm});
        }
        {
            var Q0;
            Q0=makeQuery(id+"F16.boolean.opBoolean","COPY",FACE,{"derivedFrom":makeQuery(id+"F16.opExtrude","CAP_FACE",FACE,{"disambiguationData":[OSD([sQuery(id+"F15.wireOp",EDGE,"E52"),sQuery(id+"F15.wireOp",EDGE,"E62"),sQuery(id+"F15.wireOp",EDGE,"E63")])],"isStart":false})});
            var sketch = newSketch(context, id + "F23", { "sketchPlane" : qUnion([Q0])});
            skLineSegment(sketch, "E91.0", {"start": v(13.63, 10) * mm, "end": v(13.63, 4.34) * mm});
            skLineSegment(sketch, "E92.0", {"start": v(13.63, 10) * mm, "end": v(12.5, 10) * mm});
            skLineSegment(sketch, "E93.0", {"start": v(12.5, 10) * mm, "end": v(13.63, 4.34) * mm});
            skSolve(sketch);
        }
        {
            var Q0;
            Q0 = qSketchRegion(id + "F23", true);
            var Q1;
            Q1=makeQuery(id+"F14.boolean.opBoolean","MERGE",FACE,{"derivedFrom":[makeQuery(id+"F1.opExtrude","SWEPT_FACE",FACE,{"disambiguationData":[OSD([sQuery(id+"F0.wireOp",EDGE,"E5"),sQuery(id+"F0.wireOp",EDGE,"E10.MirrorCS")])]}),makeQuery(id+"F14.opExtrude","SWEPT_FACE",FACE,{"disambiguationData":[OSD([sQuery(id+"F13.wireOp",EDGE,"E45.0.6")])]})]});
            extrude(context, id + "F24", {"entities" : qUnion([Q0]), "operationType" : NewBodyOperationType.REMOVE, "endBound" : BoundingType.UP_TO_SURFACE, "oppositeDirection" : true, "depth" : 25 * mm, "endBoundEntityFace" : qUnion([Q1]), "offsetDistance" : 25 * mm});
        }
        {
            var Q0;
            Q0=qCreatedBy(makeId("Front.planeOp"),FACE);
            var sketch = newSketch(context, id + "F25", { "sketchPlane" : qUnion([Q0])});
            skLineSegment(sketch, "E94.0", {"start": v(-35.5, 10) * mm, "end": v(-35.5, 0) * mm});
            skLineSegment(sketch, "E95", {"start": v(-35.5, 10) * mm, "end": v(-32.5, 10) * mm});
            skLineSegment(sketch, "E96", {"start": v(-32.5, 10) * mm, "end": v(-35.5, 0) * mm});
            skSolve(sketch);
        }
        {
            var Q0;
            Q0 = qSketchRegion(id + "F25", true);
            extrude(context, id + "F26", {"entities" : qUnion([Q0]), "operationType" : NewBodyOperationType.REMOVE, "endBound" : BoundingType.THROUGH_ALL, "oppositeDirection" : true, "depth" : 25 * mm, "offsetDistance" : 25 * mm, "hasSecondDirection" : true, "secondDirectionBound" : SecondDirectionBoundingType.THROUGH_ALL, "secondDirectionOppositeDirection" : false, "secondDirectionDepth" : 25 * mm});
        }
        {
            var Q0;
            Q0=makeQuery(id+"F14.opExtrude","CAP_FACE",FACE,{"disambiguationData":[OSD([sQuery(id+"F13.wireOp",EDGE,"E45.0.3"),sQuery(id+"F13.wireOp",EDGE,"E45.0.4"),sQuery(id+"F13.wireOp",EDGE,"E45.0.5"),sQuery(id+"F13.wireOp",EDGE,"E45.0.6"),sQuery(id+"F13.wireOp",EDGE,"E45.0.7"),sQuery(id+"F13.wireOp",EDGE,"E45.0.8"),sQuery(id+"F13.wireOp",EDGE,"E45.0.9"),sQuery(id+"F13.wireOp",EDGE,"E46")])],"isStart":false});
            var sketch = newSketch(context, id + "F27", { "sketchPlane" : qUnion([Q0])});
            skPoint(sketch, "E97.0", {"position": v(-31.5, 7.5) * mm});
            skPoint(sketch, "E98.0", {"position": v(-19.5, 11.5) * mm});
            skLineSegment(sketch, "E99", {"start": v(-31.5, 7.5) * mm, "end": v(-19.5, 11.5) * mm});
            skLineSegment(sketch, "E100.0", {"start": v(-31.5, 7.5) * mm, "end": v(-19.5, 10.5) * mm});
            skLineSegment(sketch, "E101.0", {"start": v(-19.5, 11.5) * mm, "end": v(-19.5, 10.5) * mm});
            skLineSegment(sketch, "E102.MirrorCS", {"start": v(-31.5, -7.5) * mm, "end": v(-19.5, -11.5) * mm});
            skLineSegment(sketch, "E103.MirrorCS", {"start": v(-31.5, -7.5) * mm, "end": v(-19.5, -10.5) * mm});
            skLineSegment(sketch, "E104.MirrorCS", {"start": v(-19.5, -11.5) * mm, "end": v(-19.5, -10.5) * mm});
            skSolve(sketch);
        }
        {
            var Q0;
            Q0 = qSketchRegion(id + "F27", true);
            var Q1;
            Q1=makeQuery(id+"F20.boolean.opBoolean","MERGE",FACE,{"derivedFrom":[makeQuery(id+"F18.boolean.opBoolean","MERGE",FACE,{"derivedFrom":[makeQuery(id+"F16.boolean.opBoolean","MERGE",FACE,{"derivedFrom":[makeQuery(id+"F1.opExtrude","CAP_FACE",FACE,{"disambiguationData":[OSD([sQuery(id+"F0.wireOp",EDGE,"E1"),sQuery(id+"F0.wireOp",EDGE,"E3"),sQuery(id+"F0.wireOp",EDGE,"E4"),sQuery(id+"F0.wireOp",EDGE,"E0.bottom"),sQuery(id+"F0.wireOp",EDGE,"E5"),sQuery(id+"F0.wireOp",EDGE,"E6"),sQuery(id+"F0.wireOp",EDGE,"E10.MirrorCS"),sQuery(id+"F0.wireOp",EDGE,"E11.MirrorCS"),sQuery(id+"F0.wireOp",EDGE,"E12.MirrorCS"),sQuery(id+"F0.wireOp",EDGE,"E13.MirrorCS"),sQuery(id+"F0.wireOp",EDGE,"E14.MirrorCS"),sQuery(id+"F0.wireOp",EDGE,"E15.MirrorCS")])],"isStart":false})],"fromTools":[makeQuery(id+"F16.opExtrude","SWEPT_FACE",FACE,{"disambiguationData":[OSD([sQuery(id+"F15.wireOp",EDGE,"E51"),sQuery(id+"F15.wireOp",EDGE,"E53"),sQuery(id+"F15.wireOp",EDGE,"E55.MirrorCS"),sQuery(id+"F15.wireOp",EDGE,"E59.MirrorCS")])]})]})],"fromTools":[makeQuery(id+"F18.opExtrude","CAP_FACE",FACE,{"disambiguationData":[OSD([sQuery(id+"F17.wireOp",EDGE,"E68"),sQuery(id+"F17.wireOp",EDGE,"E72"),sQuery(id+"F17.wireOp",EDGE,"E73"),sQuery(id+"F17.wireOp",EDGE,"E74.MirrorCS"),sQuery(id+"F17.wireOp",EDGE,"E75.MirrorCS"),sQuery(id+"F17.wireOp",EDGE,"E76.MirrorCS")])],"isStart":true})]})],"fromTools":[makeQuery(id+"F20.opExtrude","CAP_FACE",FACE,{"disambiguationData":[OSD([sQuery(id+"F19.wireOp",EDGE,"E79.0"),sQuery(id+"F19.wireOp",EDGE,"E80"),sQuery(id+"F19.wireOp",EDGE,"E81"),sQuery(id+"F19.wireOp",EDGE,"E83")])],"isStart":true}),makeQuery(id+"F20.opExtrude","CAP_FACE",FACE,{"disambiguationData":[OSD([sQuery(id+"F19.wireOp",EDGE,"E84.MirrorCS"),sQuery(id+"F19.wireOp",EDGE,"E85.MirrorCS"),sQuery(id+"F19.wireOp",EDGE,"E86.MirrorCS"),sQuery(id+"F19.wireOp",EDGE,"E87.MirrorCS")])],"isStart":true})]});
            extrude(context, id + "F28", {"entities" : qUnion([Q0]), "operationType" : NewBodyOperationType.REMOVE, "endBound" : BoundingType.UP_TO_SURFACE, "oppositeDirection" : true, "depth" : 25 * mm, "endBoundEntityFace" : qUnion([Q1]), "offsetDistance" : 25 * mm});
        }
        {
            var Q0;
            {var subQ9=sQuery(id+"F0.wireOp",EDGE,"E3");Q0=makeQuery(id+"F10.imprint","IMPRINT",FACE,{"disambiguationData":[TD([[makeQuery(id+"F10.imprint","IMPRINT",EDGE,{"derivedFrom":makeQuery(id+"F1.opExtrude","CAP_EDGE",EDGE,{"disambiguationData":[OSD([subQ9])],"isStart":false})}),1.0]])]});}
            var sketch = newSketch(context, id + "F29", { "sketchPlane" : qUnion([Q0])});
            skLineSegment(sketch, "E105.0.2", {"start": v(-31.5, 7.5) * mm, "end": v(-19.5, 11.5) * mm});
            skLineSegment(sketch, "E106", {"start": v(-31.5, 7.5) * mm, "end": v(-31.5, 8.5) * mm});
            skLineSegment(sketch, "E107", {"start": v(-19.5, 11.5) * mm, "end": v(-19.5, 12.5) * mm});
            skLineSegment(sketch, "E108", {"start": v(-19.5, 12.5) * mm, "end": v(-31.5, 8.5) * mm});
            skPoint(sketch, "E105.0.4.end.orphan", {"position": v(28.5, 12.5) * mm});
            skPoint(sketch, "E105.0.4.start.orphan", {"position": v(28.5, 11.5) * mm});
            skPoint(sketch, "E105.0.5.end.orphan", {"position": v(-23.4, 12.5) * mm});
            skPoint(sketch, "E105.0.7.start.orphan", {"position": v(-32.5, 9.87) * mm});
            skPoint(sketch, "E105.0.0.end.orphan", {"position": v(-31.5, -7.5) * mm});
            skPoint(sketch, "E105.0.8.start.orphan", {"position": v(-32.5, -9.87) * mm});
            skPoint(sketch, "E105.0.11.end.orphan", {"position": v(-19.5, -11.5) * mm});
            skPoint(sketch, "E105.0.9.start.orphan", {"position": v(-23.4, -12.5) * mm});
            skPoint(sketch, "E105.0.10.end.orphan", {"position": v(28.5, -11.5) * mm});
            skPoint(sketch, "E105.0.10.start.orphan", {"position": v(28.5, -12.5) * mm});
            skLineSegment(sketch, "E109.MirrorCS", {"start": v(-19.5, -12.5) * mm, "end": v(-31.5, -8.5) * mm});
            skLineSegment(sketch, "E110.MirrorCS", {"start": v(-31.5, -7.5) * mm, "end": v(-19.5, -11.5) * mm});
            skLineSegment(sketch, "E111.MirrorCS", {"start": v(-19.5, -11.5) * mm, "end": v(-19.5, -12.5) * mm});
            skLineSegment(sketch, "E112.MirrorCS", {"start": v(-31.5, -7.5) * mm, "end": v(-31.5, -8.5) * mm});
            skSolve(sketch);
        }
        {
            var Q0;
            Q0 = qSketchRegion(id + "F29", true);
            extrude(context, id + "F30", {"entities" : qUnion([Q0]), "operationType" : NewBodyOperationType.REMOVE, "depth" : 3 * mm, "offsetDistance" : 25 * mm});
        }
        {
            var Q0;
            Q0=qCreatedBy(makeId("Front.planeOp"),FACE);
            var sketch = newSketch(context, id + "F31", { "sketchPlane" : qUnion([Q0])});
            skPoint(sketch, "E113.0", {"position": v(-35.5, 0) * mm});
            skLineSegment(sketch, "E114", {"start": v(-35.5, 0) * mm, "end": v(-35.5, 30.8) * mm});
            skSolve(sketch);
        }
        {
            var Q0;
            Q0=sQuery(id+"F31.wireOp",EDGE,"E114");
            cPlane(context, id + "F32", {"entities" : qUnion([Q0]), "cplaneType" : CPlaneType.LINE_ANGLE, "offset" : 35 * mm, "angle" : 30 * degree, "oppositeDirection" : true, "width" : 150 * mm, "height" : 150 * mm});
        }
        {
            var Q0;
            Q0=qCreatedBy(id+"F32.planeOp",FACE);
            var sketch = newSketch(context, id + "F33", { "sketchPlane" : qUnion([Q0])});
            skPoint(sketch, "E115.0", {"position": v(-22.25, 10) * mm});
            skPoint(sketch, "E116.0", {"position": v(-24.8, 10) * mm});
            skPoint(sketch, "E117.0", {"position": v(-25.54, 0) * mm});
            skLineSegment(sketch, "E118", {"start": v(-22.25, 10) * mm, "end": v(-24.8, 10) * mm});
            skLineSegment(sketch, "E119", {"start": v(-25.54, 0) * mm, "end": v(-24.8, 10) * mm});
            skLineSegment(sketch, "E120", {"start": v(-22.66, 10) * mm, "end": v(-25.54, 0) * mm});
            skSolve(sketch);
        }
        {
            var Q0;
            Q0 = qSketchRegion(id + "F33", true);
            extrude(context, id + "F34", {"entities" : qUnion([Q0]), "operationType" : NewBodyOperationType.REMOVE, "depth" : 25 * mm, "offsetDistance" : 25 * mm});
        }
        {
            var Q0;
            Q0 = qBodyType(qCreatedBy(id + "F31" ,EDGE), BodyType.WIRE);
            cPlane(context, id + "F35", {"entities" : qUnion([Q0]), "cplaneType" : CPlaneType.LINE_ANGLE, "offset" : 25 * mm, "angle" : 210 * degree, "width" : 150 * mm, "height" : 150 * mm});
        }
        {
            var Q0;
            Q0=qCreatedBy(id+"F35.planeOp",FACE);
            var sketch = newSketch(context, id + "F36", { "sketchPlane" : qUnion([Q0])});
            skPoint(sketch, "E121.0", {"position": v(-22.25, 10) * mm});
            skPoint(sketch, "E122.0", {"position": v(-24.8, 10) * mm});
            skPoint(sketch, "E123.0", {"position": v(-25.54, 0) * mm});
            skLineSegment(sketch, "E124", {"start": v(-23.02, 10) * mm, "end": v(-24.8, 10) * mm});
            skLineSegment(sketch, "E125", {"start": v(-25.54, 0) * mm, "end": v(-24.8, 10) * mm});
            skLineSegment(sketch, "E126", {"start": v(-25.54, 0) * mm, "end": v(-23.02, 10) * mm});
            skSolve(sketch);
        }
        {
            var Q0;
            Q0 = qSketchRegion(id + "F36", true);
            extrude(context, id + "F37", {"entities" : qUnion([Q0]), "operationType" : NewBodyOperationType.REMOVE, "oppositeDirection" : true, "depth" : 25 * mm, "offsetDistance" : 25 * mm});
        }
        {
            var Q0;
            Q0=makeQuery(id+"F16.boolean.opBoolean","MERGE",EDGE,{"derivedFrom":[makeQuery(id+"F1.opExtrude","CAP_EDGE",EDGE,{"disambiguationData":[OSD([sQuery(id+"F0.wireOp",EDGE,"E12.MirrorCS")])],"isStart":true}),makeQuery(id+"F16.opExtrude","SWEPT_EDGE",EDGE,{"disambiguationData":[OSD([sQuery(id+"F0.wireOp",EDGE,"E13.MirrorCS"),sQuery(id+"F15.wireOp",EDGE,"E65.MirrorCS"),sQuery(id+"F15.wireOp",EDGE,"E66.MirrorCS")])]})]});
            var Q1;
            Q1=makeQuery(id+"F1.opExtrude","CAP_EDGE",EDGE,{"disambiguationData":[OSD([sQuery(id+"F0.wireOp",EDGE,"E11.MirrorCS")])],"isStart":true});
            var Q2;
            Q2=makeQuery(id+"F26.boolean.opBoolean","MERGE",EDGE,{"derivedFrom":[makeQuery(id+"F1.opExtrude","CAP_EDGE",EDGE,{"disambiguationData":[OSD([sQuery(id+"F0.wireOp",EDGE,"E5"),sQuery(id+"F0.wireOp",EDGE,"E10.MirrorCS")])],"isStart":true}),makeQuery(id+"F26.opExtrude","SWEPT_EDGE",EDGE,{"disambiguationData":[OSD([sQuery(id+"F25.wireOp",EDGE,"E94.0"),sQuery(id+"F25.wireOp",EDGE,"E96")])]})]});
            var Q3;
            Q3=makeQuery(id+"F1.opExtrude","CAP_EDGE",EDGE,{"disambiguationData":[OSD([sQuery(id+"F0.wireOp",EDGE,"E6")])],"isStart":true});
            var Q4;
            Q4=makeQuery(id+"F16.boolean.opBoolean","MERGE",EDGE,{"derivedFrom":[makeQuery(id+"F1.opExtrude","CAP_EDGE",EDGE,{"disambiguationData":[OSD([sQuery(id+"F0.wireOp",EDGE,"E0.bottom")])],"isStart":true}),makeQuery(id+"F16.opExtrude","SWEPT_EDGE",EDGE,{"disambiguationData":[OSD([sQuery(id+"F0.wireOp",EDGE,"E4"),sQuery(id+"F15.wireOp",EDGE,"E52"),sQuery(id+"F15.wireOp",EDGE,"E62")])]})]});
            var Q5;
            Q5=makeQuery(id+"F1.opExtrude","CAP_EDGE",EDGE,{"disambiguationData":[OSD([sQuery(id+"F0.wireOp",EDGE,"E4")])],"isStart":true});
            fillet(context, id + "F38", {"entities" : qUnion([Q0, Q1, Q2, Q3, Q4, Q5]), "radius" : 1 * mm, "tangentPropagation" : true, "allowEdgeOverflow" : false});
        }
        {
            var Q0;
            Q0=makeQuery(id+"F37.boolean.opBoolean","INTERSECT",EDGE,{"derivedFrom":[makeQuery(id+"F26.boolean.opBoolean","COPY",FACE,{"derivedFrom":makeQuery(id+"F26.opExtrude","SWEPT_FACE",FACE,{"disambiguationData":[OSD([sQuery(id+"F25.wireOp",EDGE,"E96")])]})}),makeQuery(id+"F37.opExtrude","SWEPT_FACE",FACE,{"disambiguationData":[OSD([sQuery(id+"F36.wireOp",EDGE,"E126")])]})]});
            var Q1;
            Q1=makeQuery(id+"F34.boolean.opBoolean","INTERSECT",EDGE,{"derivedFrom":[makeQuery(id+"F26.boolean.opBoolean","COPY",FACE,{"derivedFrom":makeQuery(id+"F26.opExtrude","SWEPT_FACE",FACE,{"disambiguationData":[OSD([sQuery(id+"F25.wireOp",EDGE,"E96")])]})}),makeQuery(id+"F34.opExtrude","SWEPT_FACE",FACE,{"disambiguationData":[OSD([sQuery(id+"F33.wireOp",EDGE,"E120")])]})]});
            fillet(context, id + "F39", {"entities" : qUnion([Q0, Q1]), "radius" : 3 * mm, "tangentPropagation" : true, "allowEdgeOverflow" : false});
        }
        {
            var Q0;
            Q0=makeQuery(id+"F34.boolean.opBoolean","INTERSECT",EDGE,{"derivedFrom":[makeQuery(id+"F14.boolean.opBoolean","MERGE",FACE,{"derivedFrom":[makeQuery(id+"F1.opExtrude","SWEPT_FACE",FACE,{"disambiguationData":[OSD([sQuery(id+"F0.wireOp",EDGE,"E11.MirrorCS")])]}),makeQuery(id+"F14.opExtrude","SWEPT_FACE",FACE,{"disambiguationData":[OSD([sQuery(id+"F13.wireOp",EDGE,"E45.0.7")])]})]}),makeQuery(id+"F34.opExtrude","SWEPT_FACE",FACE,{"disambiguationData":[OSD([sQuery(id+"F33.wireOp",EDGE,"E120")])]})]});
            var Q1;
            Q1=makeQuery(id+"F22.boolean.opBoolean","INTERSECT",EDGE,{"derivedFrom":[makeQuery(id+"F14.boolean.opBoolean","MERGE",FACE,{"derivedFrom":[makeQuery(id+"F1.opExtrude","SWEPT_FACE",FACE,{"disambiguationData":[OSD([sQuery(id+"F0.wireOp",EDGE,"E11.MirrorCS")])]}),makeQuery(id+"F14.opExtrude","SWEPT_FACE",FACE,{"disambiguationData":[OSD([sQuery(id+"F13.wireOp",EDGE,"E45.0.7")])]})]}),makeQuery(id+"F22.opExtrude","SWEPT_FACE",FACE,{"disambiguationData":[OSD([sQuery(id+"F21.wireOp",EDGE,"E90.0")])]})]});
            fillet(context, id + "F40", {"entities" : qUnion([Q0, Q1]), "radius" : 1 * mm, "tangentPropagation" : true, "allowEdgeOverflow" : false});
        }
        {
            var Q0;
            Q0=makeQuery(id+"F24.boolean.opBoolean","INTERSECT",EDGE,{"derivedFrom":[makeQuery(id+"F14.boolean.opBoolean","MERGE",FACE,{"derivedFrom":[makeQuery(id+"F1.opExtrude","SWEPT_FACE",FACE,{"disambiguationData":[OSD([sQuery(id+"F0.wireOp",EDGE,"E6")])]}),makeQuery(id+"F14.opExtrude","SWEPT_FACE",FACE,{"disambiguationData":[OSD([sQuery(id+"F13.wireOp",EDGE,"E45.0.5")])]})]}),makeQuery(id+"F24.opExtrude","SWEPT_FACE",FACE,{"disambiguationData":[OSD([sQuery(id+"F23.wireOp",EDGE,"E93.0")])]})]});
            var Q1;
            Q1=makeQuery(id+"F37.boolean.opBoolean","INTERSECT",EDGE,{"derivedFrom":[makeQuery(id+"F14.boolean.opBoolean","MERGE",FACE,{"derivedFrom":[makeQuery(id+"F1.opExtrude","SWEPT_FACE",FACE,{"disambiguationData":[OSD([sQuery(id+"F0.wireOp",EDGE,"E6")])]}),makeQuery(id+"F14.opExtrude","SWEPT_FACE",FACE,{"disambiguationData":[OSD([sQuery(id+"F13.wireOp",EDGE,"E45.0.5")])]})]}),makeQuery(id+"F37.opExtrude","SWEPT_FACE",FACE,{"disambiguationData":[OSD([sQuery(id+"F36.wireOp",EDGE,"E126")])]})]});
            fillet(context, id + "F41", {"entities" : qUnion([Q0, Q1]), "radius" : 1 * mm, "tangentPropagation" : true, "allowEdgeOverflow" : false});
        }
        {
            var Q0;
            {var subQ0=sQuery(id+"F15.wireOp",EDGE,"E58.MirrorCS");Q0=makeQuery(id+"F28.boolean.opBoolean","MERGE",EDGE,{"derivedFrom":[makeQuery(id+"F16.boolean.opBoolean","COPY",EDGE,{"derivedFrom":makeQuery(id+"F16.opExtrude","CAP_EDGE",EDGE,{"disambiguationData":[OSD([subQ0])],"isStart":false})})],"fromTools":[makeQuery(id+"F28.opExtrude","SWEPT_EDGE",EDGE,{"disambiguationData":[OSD([sQuery(id+"F13.wireOp",EDGE,"E45.0.3"),sQuery(id+"F13.wireOp",EDGE,"E45.0.9"),sQuery(id+"F13.wireOp",EDGE,"E46"),sQuery(id+"F15.wireOp",EDGE,"E54.MirrorCS"),subQ0,sQuery(id+"F27.wireOp",EDGE,"E102.MirrorCS"),sQuery(id+"F27.wireOp",EDGE,"E104.MirrorCS")])]})]});}
            var Q1;
            Q1=makeQuery(id+"F30.boolean.opBoolean","MERGE",EDGE,{"derivedFrom":[makeQuery(id+"F16.boolean.opBoolean","COPY",EDGE,{"derivedFrom":makeQuery(id+"F16.opExtrude","CAP_EDGE",EDGE,{"disambiguationData":[OSD([sQuery(id+"F15.wireOp",EDGE,"E56.MirrorCS")])],"isStart":false})}),makeQuery(id+"F30.opExtrude","SWEPT_EDGE",EDGE,{"disambiguationData":[OSD([sQuery(id+"F29.wireOp",EDGE,"E109.MirrorCS"),sQuery(id+"F29.wireOp",EDGE,"E111.MirrorCS")])]})]});
            var Q2;
            Q2=makeQuery(id+"F30.boolean.opBoolean","MERGE",EDGE,{"derivedFrom":[makeQuery(id+"F20.boolean.opBoolean","COPY",EDGE,{"derivedFrom":makeQuery(id+"F20.opExtrude","SWEPT_EDGE",EDGE,{"disambiguationData":[OSD([sQuery(id+"F19.wireOp",EDGE,"E85.MirrorCS"),sQuery(id+"F19.wireOp",EDGE,"E87.MirrorCS")])]})}),makeQuery(id+"F30.opExtrude","SWEPT_EDGE",EDGE,{"disambiguationData":[OSD([sQuery(id+"F29.wireOp",EDGE,"E109.MirrorCS"),sQuery(id+"F29.wireOp",EDGE,"E112.MirrorCS")])]})]});
            var Q3;
            {var subQ0=sQuery(id+"F17.wireOp",EDGE,"E76.MirrorCS");Q3=makeQuery(id+"F28.boolean.opBoolean","MERGE",EDGE,{"derivedFrom":[makeQuery(id+"F18.boolean.opBoolean","COPY",EDGE,{"derivedFrom":makeQuery(id+"F18.opExtrude","SWEPT_EDGE",EDGE,{"disambiguationData":[OSD([sQuery(id+"F17.wireOp",EDGE,"E74.MirrorCS"),subQ0])]})})],"fromTools":[makeQuery(id+"F28.opExtrude","SWEPT_EDGE",EDGE,{"disambiguationData":[OSD([sQuery(id+"F17.wireOp",EDGE,"E72"),subQ0,sQuery(id+"F27.wireOp",EDGE,"E102.MirrorCS"),sQuery(id+"F27.wireOp",EDGE,"E103.MirrorCS")])]})]});}
            var Q4;
            {var subQ0=sQuery(id+"F17.wireOp",EDGE,"E72");Q4=makeQuery(id+"F28.boolean.opBoolean","MERGE",EDGE,{"derivedFrom":[makeQuery(id+"F18.boolean.opBoolean","COPY",EDGE,{"derivedFrom":makeQuery(id+"F18.opExtrude","SWEPT_EDGE",EDGE,{"disambiguationData":[OSD([subQ0,sQuery(id+"F17.wireOp",EDGE,"E73")])]})})],"fromTools":[makeQuery(id+"F28.opExtrude","SWEPT_EDGE",EDGE,{"disambiguationData":[OSD([subQ0,sQuery(id+"F17.wireOp",EDGE,"E76.MirrorCS"),sQuery(id+"F27.wireOp",EDGE,"E99"),sQuery(id+"F27.wireOp",EDGE,"E100.0")])]})]});}
            var Q5;
            Q5=makeQuery(id+"F30.boolean.opBoolean","MERGE",EDGE,{"derivedFrom":[makeQuery(id+"F20.boolean.opBoolean","COPY",EDGE,{"derivedFrom":makeQuery(id+"F20.opExtrude","SWEPT_EDGE",EDGE,{"disambiguationData":[OSD([sQuery(id+"F19.wireOp",EDGE,"E81"),sQuery(id+"F19.wireOp",EDGE,"E83")])]})}),makeQuery(id+"F30.opExtrude","SWEPT_EDGE",EDGE,{"disambiguationData":[OSD([sQuery(id+"F29.wireOp",EDGE,"E106"),sQuery(id+"F29.wireOp",EDGE,"E108")])]})]});
            var Q6;
            {var subQ0=sQuery(id+"F15.wireOp",EDGE,"E48");Q6=makeQuery(id+"F28.boolean.opBoolean","MERGE",EDGE,{"derivedFrom":[makeQuery(id+"F16.boolean.opBoolean","COPY",EDGE,{"derivedFrom":makeQuery(id+"F16.opExtrude","CAP_EDGE",EDGE,{"disambiguationData":[OSD([subQ0])],"isStart":false})})],"fromTools":[makeQuery(id+"F28.opExtrude","SWEPT_EDGE",EDGE,{"disambiguationData":[OSD([sQuery(id+"F13.wireOp",EDGE,"E45.0.3"),sQuery(id+"F13.wireOp",EDGE,"E45.0.9"),sQuery(id+"F13.wireOp",EDGE,"E46"),sQuery(id+"F15.wireOp",EDGE,"E47"),subQ0,sQuery(id+"F27.wireOp",EDGE,"E99"),sQuery(id+"F27.wireOp",EDGE,"E101.0")])]})]});}
            var Q7;
            Q7=makeQuery(id+"F30.boolean.opBoolean","MERGE",EDGE,{"derivedFrom":[makeQuery(id+"F16.boolean.opBoolean","COPY",EDGE,{"derivedFrom":makeQuery(id+"F16.opExtrude","CAP_EDGE",EDGE,{"disambiguationData":[OSD([sQuery(id+"F15.wireOp",EDGE,"E50")])],"isStart":false})}),makeQuery(id+"F30.opExtrude","SWEPT_EDGE",EDGE,{"disambiguationData":[OSD([sQuery(id+"F29.wireOp",EDGE,"E107"),sQuery(id+"F29.wireOp",EDGE,"E108")])]})]});
            fillet(context, id + "F42", {"entities" : qUnion([Q0, Q1, Q2, Q3, Q4, Q5, Q6, Q7]), "radius" : 1 * mm, "tangentPropagation" : true, "allowEdgeOverflow" : false});
        }
        {
            var Q0;
            Q0=makeQuery(id+"F14.opExtrude","CAP_FACE",FACE,{"disambiguationData":[OSD([sQuery(id+"F13.wireOp",EDGE,"E45.0.3"),sQuery(id+"F13.wireOp",EDGE,"E45.0.4"),sQuery(id+"F13.wireOp",EDGE,"E45.0.5"),sQuery(id+"F13.wireOp",EDGE,"E45.0.6"),sQuery(id+"F13.wireOp",EDGE,"E45.0.7"),sQuery(id+"F13.wireOp",EDGE,"E45.0.8"),sQuery(id+"F13.wireOp",EDGE,"E45.0.9"),sQuery(id+"F13.wireOp",EDGE,"E46")])],"isStart":false});
            var sketch = newSketch(context, id + "F43", { "sketchPlane" : qUnion([Q0])});
            skLineSegment(sketch, "E127", {"start": v(-30.82, 7.73) * mm, "end": v(-19.65, 11.45) * mm});
            skLineSegment(sketch, "E128", {"start": v(-30.82, 7.73) * mm, "end": v(-28.27, 9.63) * mm});
            skPoint(sketch, "E128.endSnap0", {"position": v(-28.27, 8.85) * mm});
            skPoint(sketch, "E129.MirrorP", {"position": v(-28.27, -8.85) * mm});
            skPoint(sketch, "E130.end.orphan", {"position": v(-20.15, 12.31) * mm});
            skPoint(sketch, "E131.MirrorCS.end.orphan", {"position": v(-28.27, -9.63) * mm});
            skPoint(sketch, "E131.MirrorCS.start.orphan", {"position": v(-30.82, -7.73) * mm});
            skPoint(sketch, "E132.MirrorCS.end.orphan", {"position": v(-20.15, -12.31) * mm});
            skPoint(sketch, "E132.MirrorCS.start.orphan", {"position": v(-19.65, -11.45) * mm});
            skLineSegment(sketch, "E133", {"start": v(-28.27, 9.63) * mm, "end": v(-19.65, 11.45) * mm});
            skLineSegment(sketch, "E134.MirrorCS", {"start": v(-30.82, -7.73) * mm, "end": v(-19.65, -11.45) * mm});
            skLineSegment(sketch, "E135.MirrorCS", {"start": v(-30.82, -7.73) * mm, "end": v(-28.27, -9.63) * mm});
            skLineSegment(sketch, "E136.MirrorCS", {"start": v(-28.27, -9.63) * mm, "end": v(-19.65, -11.45) * mm});
            skSolve(sketch);
        }
        {
            var Q0;
            Q0 = qSketchRegion(id + "F43", true);
            var Q1;
            Q1=makeQuery(id+"F30.boolean.opBoolean","MERGE",FACE,{"derivedFrom":[makeQuery(id+"F16.boolean.opBoolean","COPY",FACE,{"derivedFrom":makeQuery(id+"F16.opExtrude","SWEPT_FACE",FACE,{"disambiguationData":[OSD([sQuery(id+"F15.wireOp",EDGE,"E49")])]})}),makeQuery(id+"F20.boolean.opBoolean","COPY",FACE,{"derivedFrom":makeQuery(id+"F20.opExtrude","CAP_FACE",FACE,{"disambiguationData":[OSD([sQuery(id+"F19.wireOp",EDGE,"E79.0"),sQuery(id+"F19.wireOp",EDGE,"E80"),sQuery(id+"F19.wireOp",EDGE,"E81"),sQuery(id+"F19.wireOp",EDGE,"E83")])],"isStart":false})}),makeQuery(id+"F30.opExtrude","CAP_FACE",FACE,{"disambiguationData":[OSD([sQuery(id+"F29.wireOp",EDGE,"E105.0.2"),sQuery(id+"F29.wireOp",EDGE,"E106"),sQuery(id+"F29.wireOp",EDGE,"E107"),sQuery(id+"F29.wireOp",EDGE,"E108")])],"isStart":false})]});
            extrude(context, id + "F44", {"entities" : qUnion([Q0]), "operationType" : NewBodyOperationType.REMOVE, "endBound" : BoundingType.UP_TO_SURFACE, "oppositeDirection" : true, "depth" : 25 * mm, "endBoundEntityFace" : qUnion([Q1]), "offsetDistance" : 25 * mm});
        }
        {
            var Q0;
            {var subQ0=sQuery(id+"F13.wireOp",EDGE,"E46");var subQ1=sQuery(id+"F13.wireOp",EDGE,"E45.0.9");var subQ2=sQuery(id+"F13.wireOp",EDGE,"E45.0.3");var subQ3=sQuery(id+"F0.wireOp",EDGE,"E14.MirrorCS");var subQ5=sQuery(id+"F0.wireOp",EDGE,"E13.MirrorCS");var subQ12=sQuery(id+"F0.wireOp",EDGE,"E4");Q0=makeQuery(id+"F16.boolean.opBoolean","SPLIT",FACE,{"disambiguationData":[TD([makeQuery(id+"F1.opExtrude","SWEPT_FACE",FACE,{"disambiguationData":[OSD([subQ3])]})])],"derivedFrom":makeQuery(id+"F14.boolean.opBoolean","MERGE",FACE,{"derivedFrom":[makeQuery(id+"F1.opExtrude","SWEPT_FACE",FACE,{"disambiguationData":[OSD([subQ12])]}),makeQuery(id+"F1.opExtrude","SWEPT_FACE",FACE,{"disambiguationData":[OSD([subQ5])]}),makeQuery(id+"F14.opExtrude","SWEPT_FACE",FACE,{"disambiguationData":[OSD([subQ2,subQ1,subQ0])]})]})});}
            var sketch = newSketch(context, id + "F45", { "sketchPlane" : qUnion([Q0])});
            skLineSegment(sketch, "E137.0.0", {"start": v(-12.5, 10) * mm, "end": v(-14.26, 1.2) * mm});
            skArc(sketch, "E137.0.1", {"start": v(-14.26, 1.2) * mm, "mid": v(-14.05, 0.37) * mm, "end": v(-13.28, 0) * mm});
            skLineSegment(sketch, "E137.0.2", {"start": v(-13.28, 0) * mm, "end": v(-9.5, 0) * mm});
            skLineSegment(sketch, "E137.0.3", {"start": v(-9.5, 0) * mm, "end": v(-9.5, 3) * mm});
            skLineSegment(sketch, "E137.0.4", {"start": v(-9.5, 3) * mm, "end": v(-12.5, 3) * mm});
            skLineSegment(sketch, "E137.0.5", {"start": v(-12.5, 3) * mm, "end": v(-12.5, 6) * mm});
            skLineSegment(sketch, "E137.0.6", {"start": v(-12.5, 6) * mm, "end": v(-11.5, 6) * mm});
            skLineSegment(sketch, "E137.0.7", {"start": v(-11.5, 6) * mm, "end": v(-11.5, 10) * mm});
            skLineSegment(sketch, "E137.0.8", {"start": v(-11.5, 10) * mm, "end": v(-12.5, 10) * mm});
            skLineSegment(sketch, "E138.MirrorCS", {"start": v(11.5, 10) * mm, "end": v(12.5, 10) * mm});
            skLineSegment(sketch, "E139.MirrorCS", {"start": v(13.28, 0) * mm, "end": v(9.5, 0) * mm});
            skLineSegment(sketch, "E140.MirrorCS", {"start": v(12.5, 3) * mm, "end": v(12.5, 6) * mm});
            skLineSegment(sketch, "E141.MirrorCS", {"start": v(9.5, 3) * mm, "end": v(12.5, 3) * mm});
            skLineSegment(sketch, "E142.MirrorCS", {"start": v(11.5, 6) * mm, "end": v(11.5, 10) * mm});
            skArc(sketch, "E143.MirrorCS", {"start": v(14.26, 1.2) * mm, "mid": v(14.05, 0.37) * mm, "end": v(13.28, 0) * mm});
            skLineSegment(sketch, "E144.MirrorCS", {"start": v(12.5, 6) * mm, "end": v(11.5, 6) * mm});
            skLineSegment(sketch, "E145.MirrorCS", {"start": v(9.5, 0) * mm, "end": v(9.5, 3) * mm});
            skLineSegment(sketch, "E146.MirrorCS", {"start": v(12.5, 10) * mm, "end": v(14.26, 1.2) * mm});
            skSolve(sketch);
        }
        {
            var Q0;
            Q0 = qSketchRegion(id + "F45", true);
            extrude(context, id + "F46", {"entities" : qUnion([Q0]), "operationType" : NewBodyOperationType.ADD, "depth" : 1 * mm, "offsetDistance" : 25 * mm});
        }
        {
            var Q0;
            Q0=makeQuery(id+"F46.opExtrude","CAP_FACE",FACE,{"disambiguationData":[OSD([sQuery(id+"F45.wireOp",EDGE,"E138.MirrorCS"),sQuery(id+"F45.wireOp",EDGE,"E139.MirrorCS"),sQuery(id+"F45.wireOp",EDGE,"E140.MirrorCS"),sQuery(id+"F45.wireOp",EDGE,"E141.MirrorCS"),sQuery(id+"F45.wireOp",EDGE,"E142.MirrorCS"),sQuery(id+"F45.wireOp",EDGE,"E143.MirrorCS"),sQuery(id+"F45.wireOp",EDGE,"E144.MirrorCS"),sQuery(id+"F45.wireOp",EDGE,"E145.MirrorCS"),sQuery(id+"F45.wireOp",EDGE,"E146.MirrorCS")])],"isStart":true});
            var sketch = newSketch(context, id + "F47", { "sketchPlane" : qUnion([Q0])});
            skLineSegment(sketch, "E147.0.0", {"start": v(-9.5, 0) * mm, "end": v(-9.5, 1) * mm});
            skLineSegment(sketch, "E147.0.1", {"start": v(-9.5, 1) * mm, "end": v(-14.28, 1) * mm});
            skArc(sketch, "E147.0.2", {"start": v(-14.28, 1) * mm, "mid": v(-13.99, 0.3) * mm, "end": v(-13.28, 0) * mm});
            skLineSegment(sketch, "E147.0.3", {"start": v(-13.28, 0) * mm, "end": v(-9.5, 0) * mm});
            skSolve(sketch);
        }
        {
            var Q0;
            Q0 = qSketchRegion(id + "F47", true);
            var Q1;
            Q1=makeQuery(id+"F38.opFillet","BLEND_FACE",FACE,{"disambiguationData":[OSD([sQuery(id+"F0.wireOp",EDGE,"E4")])]});
            extrude(context, id + "F48", {"entities" : qUnion([Q0]), "operationType" : NewBodyOperationType.ADD, "endBound" : BoundingType.UP_TO_SURFACE, "depth" : 25 * mm, "endBoundEntityFace" : qUnion([Q1]), "offsetDistance" : 25 * mm});
        }
        {
            var Q0;
            Q0=makeQuery(id+"F46.opExtrude","CAP_FACE",FACE,{"disambiguationData":[OSD([sQuery(id+"F45.wireOp",EDGE,"E137.0.0"),sQuery(id+"F45.wireOp",EDGE,"E137.0.1"),sQuery(id+"F45.wireOp",EDGE,"E137.0.2"),sQuery(id+"F45.wireOp",EDGE,"E137.0.3"),sQuery(id+"F45.wireOp",EDGE,"E137.0.4"),sQuery(id+"F45.wireOp",EDGE,"E137.0.5"),sQuery(id+"F45.wireOp",EDGE,"E137.0.6"),sQuery(id+"F45.wireOp",EDGE,"E137.0.7"),sQuery(id+"F45.wireOp",EDGE,"E137.0.8")])],"isStart":false});
            var sketch = newSketch(context, id + "F49", { "sketchPlane" : qUnion([Q0])});
            skLineSegment(sketch, "E148", {"start": v(-11.5, 10) * mm, "end": v(-11.5, 6) * mm});
            skLineSegment(sketch, "E149", {"start": v(-11.5, 6) * mm, "end": v(-13.3, 6) * mm});
            skLineSegment(sketch, "E150", {"start": v(-13.3, 6) * mm, "end": v(-12.5, 10) * mm});
            skLineSegment(sketch, "E151", {"start": v(-12.5, 10) * mm, "end": v(-11.5, 10) * mm});
            skLineSegment(sketch, "E152.MirrorCS", {"start": v(11.5, 10) * mm, "end": v(11.5, 6) * mm});
            skLineSegment(sketch, "E153.MirrorCS", {"start": v(12.5, 10) * mm, "end": v(11.5, 10) * mm});
            skLineSegment(sketch, "E154.MirrorCS", {"start": v(11.5, 6) * mm, "end": v(13.3, 6) * mm});
            skLineSegment(sketch, "E155.MirrorCS", {"start": v(13.3, 6) * mm, "end": v(12.5, 10) * mm});
            skSolve(sketch);
        }
        {
            var Q0;
            Q0 = qSketchRegion(id + "F49", true);
            extrude(context, id + "F50", {"entities" : qUnion([Q0]), "operationType" : NewBodyOperationType.ADD, "depth" : 1 * mm, "offsetDistance" : 25 * mm});
        }
        {
            var Q0;
            Q0=makeQuery(id+"F1.opExtrude","SWEPT_EDGE",EDGE,{"disambiguationData":[OSD([sQuery(id+"F0.wireOp",EDGE,"E13.MirrorCS"),sQuery(id+"F0.wireOp",EDGE,"E14.MirrorCS")])]});
            var Q1;
            Q1=makeQuery(id+"F1.opExtrude","SWEPT_EDGE",EDGE,{"disambiguationData":[OSD([sQuery(id+"F0.wireOp",EDGE,"E14.MirrorCS"),sQuery(id+"F0.wireOp",EDGE,"E15.MirrorCS")])]});
            var Q2;
            Q2=makeQuery(id+"F1.opExtrude","SWEPT_EDGE",EDGE,{"disambiguationData":[OSD([sQuery(id+"F0.wireOp",EDGE,"E1"),sQuery(id+"F0.wireOp",EDGE,"E3")])]});
            var Q3;
            Q3=makeQuery(id+"F1.opExtrude","SWEPT_EDGE",EDGE,{"disambiguationData":[OSD([sQuery(id+"F0.wireOp",EDGE,"E3"),sQuery(id+"F0.wireOp",EDGE,"E4")])]});
            fillet(context, id + "F51", {"entities" : qUnion([Q0, Q1, Q2, Q3]), "radius" : 3 * mm, "tangentPropagation" : true, "allowEdgeOverflow" : false});
        }
        {
            var Q0;
            Q0=makeQuery(id+"F46.opExtrude","CAP_EDGE",EDGE,{"disambiguationData":[OSD([sQuery(id+"F45.wireOp",EDGE,"E137.0.1")])],"isStart":false});
            var Q1;
            Q1=makeQuery(id+"F46.opExtrude","CAP_EDGE",EDGE,{"disambiguationData":[OSD([sQuery(id+"F45.wireOp",EDGE,"E143.MirrorCS")])],"isStart":false});
            var Q2;
            Q2=makeQuery(id+"F50.opExtrude","CAP_EDGE",EDGE,{"disambiguationData":[OSD([sQuery(id+"F49.wireOp",EDGE,"E150")])],"isStart":false});
            var Q3;
            Q3=makeQuery(id+"F50.opExtrude","CAP_EDGE",EDGE,{"disambiguationData":[OSD([sQuery(id+"F49.wireOp",EDGE,"E155.MirrorCS")])],"isStart":false});
            fillet(context, id + "F52", {"entities" : qUnion([Q0, Q1, Q2, Q3]), "radius" : 1 * mm, "tangentPropagation" : true, "allowEdgeOverflow" : false});
        }
    });
